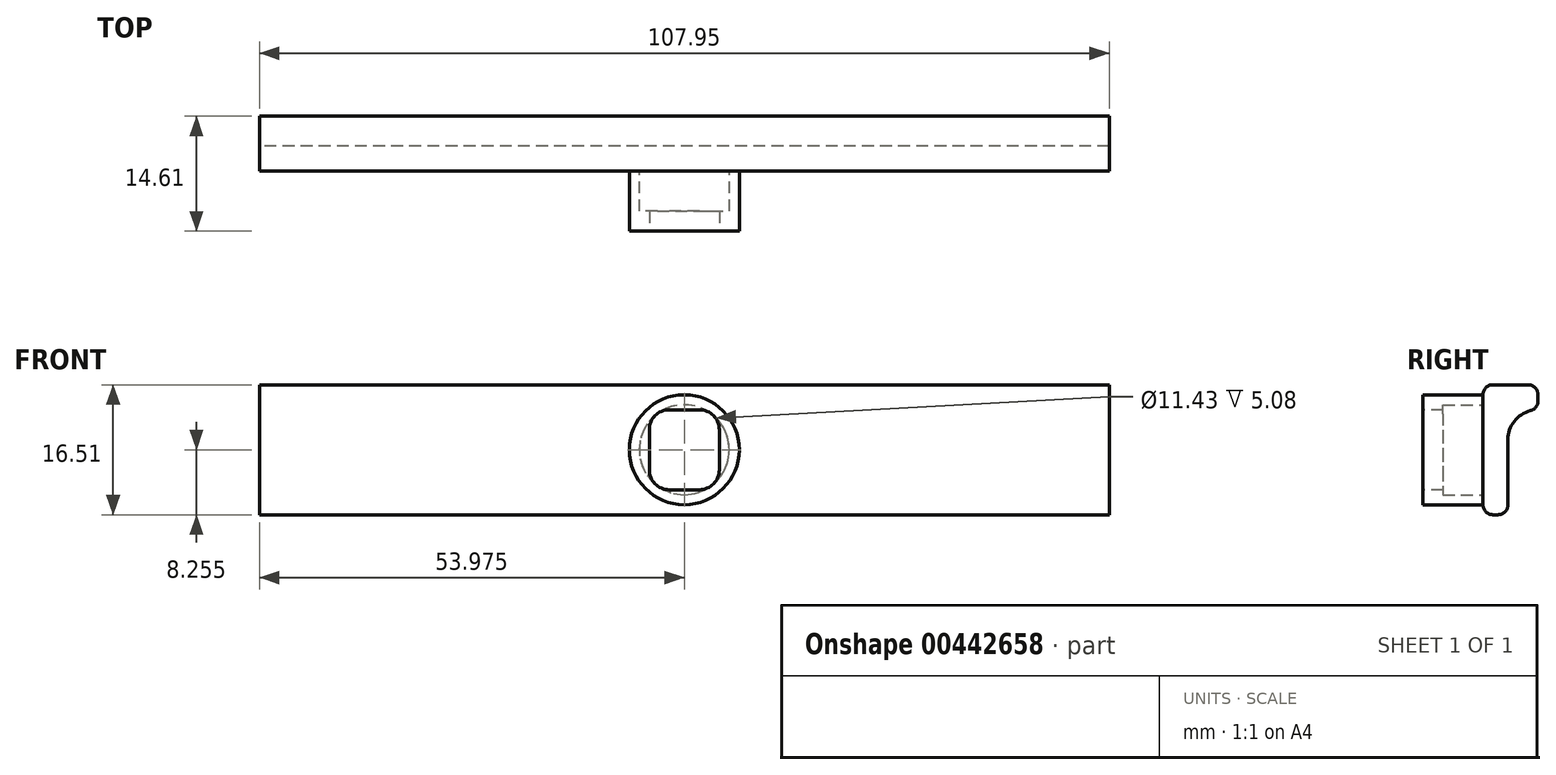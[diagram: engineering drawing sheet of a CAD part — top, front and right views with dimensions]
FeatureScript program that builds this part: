
annotation { "Feature Type Name" : "Feature", "Feature Type Description" : "" }
export const myFeature = defineFeature(function(context is Context, id is Id, definition is map)
    precondition{}
    {
        {
            var Q0;
            Q0=qCreatedBy(makeId("Right.planeOp"),FACE);
            var sketch = newSketch(context, id + "F0", { "sketchPlane" : qUnion([Q0])});
            skLineSegment(sketch, "E0", {"start": v(0, 1.27) * mm, "end": v(0, 10.16) * mm});
            skLineSegment(sketch, "E1", {"start": v(1.27, 0) * mm, "end": v(1.9, 0) * mm});
            skLineSegment(sketch, "E2", {"start": v(6.99, 15.24) * mm, "end": v(6.99, 14.44) * mm});
            skLineSegment(sketch, "E3", {"start": v(0, 10.16) * mm, "end": v(0, 15.24) * mm});
            skPoint(sketch, "E4.orphan", {"position": v(8.34, 13.34) * mm});
            skPoint(sketch, "E5.orphan", {"position": v(3.05, 10.16) * mm});
            skLineSegment(sketch, "E6", {"start": v(3.18, 1.27) * mm, "end": v(3.18, 9.53) * mm});
            skPoint(sketch, "E7.end.orphan", {"position": v(2.36, 13.34) * mm});
            skLineSegment(sketch, "E8", {"start": v(6.99, 13.34) * mm, "end": v(6.99, 13.34) * mm});
            skLineSegment(sketch, "E9", {"start": v(1.27, 16.51) * mm, "end": v(5.72, 16.51) * mm});
            skPoint(sketch, "E10.visualSharp", {"position": v(3.17, 13.34) * mm});
            skArc(sketch, "E10.filletArc", {"start": v(6.03, 13.21) * mm, "mid": v(3.97, 11.86) * mm, "end": v(3.17, 9.53) * mm});
            skPoint(sketch, "E11.visualSharp", {"position": v(6.99, 16.51) * mm});
            skArc(sketch, "E11.filletArc", {"start": v(6.99, 15.24) * mm, "mid": v(6.61, 16.14) * mm, "end": v(5.72, 16.51) * mm});
            skPoint(sketch, "E12.visualSharp", {"position": v(0, 16.51) * mm});
            skArc(sketch, "E12.filletArc", {"start": v(1.27, 16.51) * mm, "mid": v(0.37, 16.14) * mm, "end": v(0, 15.24) * mm});
            skPoint(sketch, "E13.visualSharp", {"position": v(3.18, 0) * mm});
            skArc(sketch, "E13.filletArc", {"start": v(1.9, 0) * mm, "mid": v(2.8, 0.37) * mm, "end": v(3.17, 1.27) * mm});
            skPoint(sketch, "E14.visualSharp", {"position": v(0, 0) * mm});
            skArc(sketch, "E14.filletArc", {"start": v(0, 1.27) * mm, "mid": v(0.37, 0.37) * mm, "end": v(1.27, 0) * mm});
            skPoint(sketch, "E15.visualSharp", {"position": v(6.99, 13.34) * mm});
            skArc(sketch, "E15.filletArc", {"start": v(6.03, 13.21) * mm, "mid": v(6.72, 13.67) * mm, "end": v(6.99, 14.44) * mm});
            skSolve(sketch);
        }
        {
            var Q0;
            Q0=makeQuery(id+"F0.imprint","IMPRINT",FACE,{"disambiguationData":[TD([[makeQuery(id+"F0.imprint","IMPRINT",EDGE,{"derivedFrom":sQuery(id+"F0.wireOp",EDGE,"E0")}),-1.0]])]});
            extrude(context, id + "F1", {"entities" : qUnion([Q0]), "depth" : 107.95 * mm});
        }
        {
            var Q0;
            Q0=makeQuery(id+"F1.opExtrude","SWEPT_FACE",FACE,{"disambiguationData":[OSD([sQuery(id+"F0.wireOp",EDGE,"E0"),sQuery(id+"F0.wireOp",EDGE,"E3")])]});
            var sketch = newSketch(context, id + "F2", { "sketchPlane" : qUnion([Q0])});
            skCircle(sketch, "E16", {"center": v(53.98, 8.26) * mm, "radius": 6.99 * mm});
            skCircle(sketch, "E17", {"center": v(53.98, 8.26) * mm, "radius": 5.72 * mm});
            skSolve(sketch);
        }
        {
            var Q0;
            Q0=makeQuery(id+"F2.imprint","IMPRINT",FACE,{"disambiguationData":[TD([[makeQuery(id+"F2.imprint","IMPRINT",EDGE,{"derivedFrom":sQuery(id+"F2.wireOp",EDGE,"E17")}),-1.0]])]});
            extrude(context, id + "F3", {"entities" : qUnion([Q0]), "operationType" : NewBodyOperationType.ADD, "depth" : 5.08 * mm});
        }
        {
            var Q0;
            Q0=makeQuery(id+"F3.opExtrude","CAP_FACE",FACE,{"disambiguationData":[OSD([sQuery(id+"F2.wireOp",EDGE,"E16"),sQuery(id+"F2.wireOp",EDGE,"E17")])],"isStart":false});
            var sketch = newSketch(context, id + "F4", { "sketchPlane" : qUnion([Q0])});
            skCircle(sketch, "E18", {"center": v(53.98, 8.26) * mm, "radius": 6.98 * mm});
            skPoint(sketch, "E18.first.point", {"position": v(51.14, 14.64) * mm});
            skPoint(sketch, "E18.second.point", {"position": v(60.88, 7.2) * mm});
            skPoint(sketch, "E18.third.point", {"position": v(49.1, 3.26) * mm});
            skSolve(sketch);
        }
        {
            var Q0;
            Q0 = qSketchRegion(id + "F4", true);
            extrude(context, id + "F5", {"entities" : qUnion([Q0]), "operationType" : NewBodyOperationType.ADD, "depth" : 2.54 * mm});
        }
        {
            var Q0;
            Q0=makeQuery(id+"F5.opExtrude","CAP_FACE",FACE,{"disambiguationData":[OSD([sQuery(id+"F4.wireOp",EDGE,"E18")])],"isStart":false});
            var sketch = newSketch(context, id + "F6", { "sketchPlane" : qUnion([Q0])});
            skLineSegment(sketch, "E19.top", {"start": v(53.98, 13.34) * mm, "end": v(55.88, 13.34) * mm});
            skLineSegment(sketch, "E19.right", {"start": v(58.42, 8.26) * mm, "end": v(58.42, 10.8) * mm});
            skLineSegment(sketch, "E20.bottom", {"start": v(55.88, 13.34) * mm, "end": v(52.07, 13.34) * mm});
            skLineSegment(sketch, "E20.top", {"start": v(55.88, 3.18) * mm, "end": v(52.07, 3.18) * mm});
            skLineSegment(sketch, "E20.left", {"start": v(58.42, 8.26) * mm, "end": v(58.42, 5.72) * mm});
            skLineSegment(sketch, "E20.right", {"start": v(49.53, 10.8) * mm, "end": v(49.53, 5.72) * mm});
            skPoint(sketch, "E21.visualSharp", {"position": v(49.53, 13.34) * mm});
            skArc(sketch, "E21.filletArc", {"start": v(52.07, 13.34) * mm, "mid": v(50.27, 12.6) * mm, "end": v(49.53, 10.8) * mm});
            skPoint(sketch, "E22.visualSharp", {"position": v(49.53, 3.18) * mm});
            skArc(sketch, "E22.filletArc", {"start": v(49.53, 5.72) * mm, "mid": v(50.27, 3.92) * mm, "end": v(52.07, 3.18) * mm});
            skPoint(sketch, "E23.visualSharp", {"position": v(58.42, 3.18) * mm});
            skArc(sketch, "E23.filletArc", {"start": v(55.88, 3.18) * mm, "mid": v(57.68, 3.92) * mm, "end": v(58.42, 5.72) * mm});
            skPoint(sketch, "E24.visualSharp", {"position": v(58.42, 13.34) * mm});
            skArc(sketch, "E24.filletArc", {"start": v(58.42, 10.8) * mm, "mid": v(57.68, 12.6) * mm, "end": v(55.88, 13.34) * mm});
            skPoint(sketch, "E19.bottom.start.orphan", {"position": v(53.98, 8.26) * mm});
            skSolve(sketch);
        }
        {
            var Q0;
            Q0=makeQuery(id+"F6.imprint","IMPRINT",FACE,{"disambiguationData":[TD([[makeQuery(id+"F6.imprint","IMPRINT",EDGE,{"derivedFrom":sQuery(id+"F6.wireOp",EDGE,"E19.right")}),1.0]])]});
            extrude(context, id + "F7", {"entities" : qUnion([Q0]), "operationType" : NewBodyOperationType.REMOVE, "oppositeDirection" : true, "depth" : 5.08 * mm});
        }
    });
